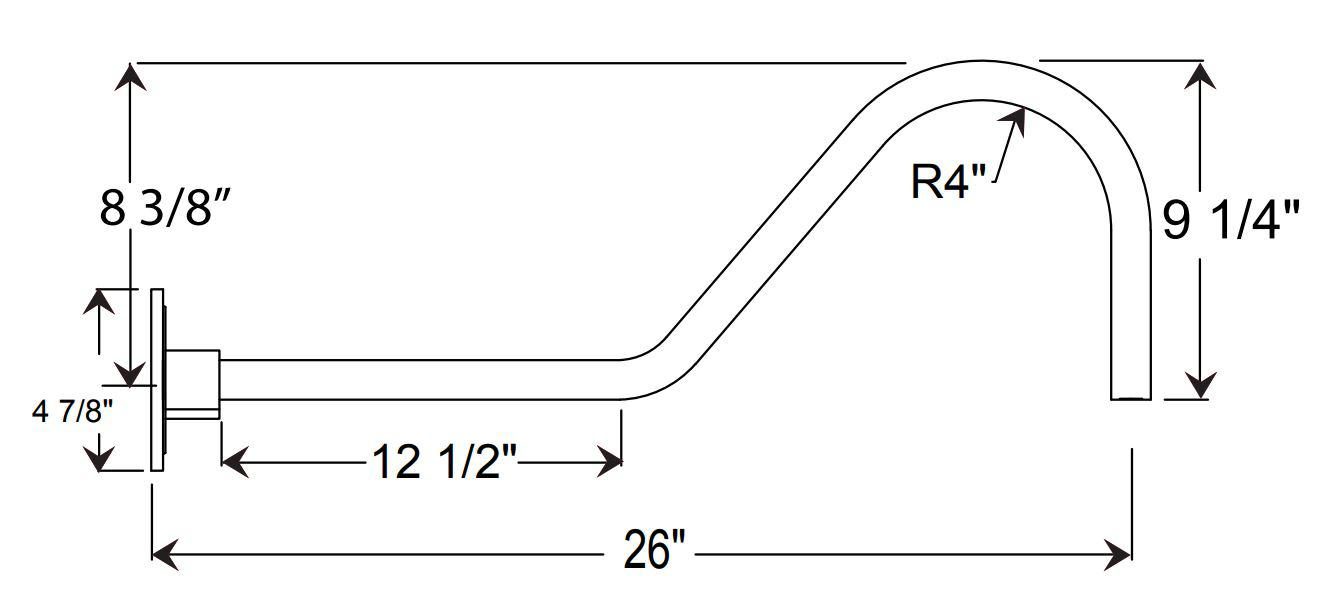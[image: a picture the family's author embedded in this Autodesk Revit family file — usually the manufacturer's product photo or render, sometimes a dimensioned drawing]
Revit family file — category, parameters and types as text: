
# Revit family: OSDC 24,36,42,48 LED
name_source: partatom
category: Lighting Fixtures
units: mm (PartAtom-declared; Revit-internal decimal feet)

## family parameters
Always vertical = Yes
Cut with Voids When Loaded = No
Light Source = Yes
OmniClass Number = 23.80.70.00
OmniClass Title = Lighting
Part Type = Normal
Room Calculation Point = No
Round Connector Dimension = Use Diameter
Shared = No
Work Plane-Based = No

## types (4) — shared parameters
Body Colour = Spun aluminium
Body Material = body
Bulb = Bulb
CRI = >90
Color Filter = 16777215
Construction Material = Heavy Duty spun aluminum.
Default Elevation = 0' - 0"
Description = 120-277 Voltage
Dimming = 1%
Dimming Lamp Color Temperature Shift = <None>
Efficiency = 65-125 lumens per watt
INSIDE BODY = INSIDE BODY
Lamp = LED
Life = L70 50,000 hours
Load Classification = Lighting
Manufacturer = ANP Lighting
Photometric Web File = OSDC48M037LDDW35K.ies
Power Factor = 1
Tilt Angle = 90.00°
URL = https://www.anplighting.com
Voltage = 277 V
Warranty = 5 year limited warranty

## per-type parameters (varying)
| type | Apparent Load | Fixture Diameter | Fixture Height | OSDC24 | OSDC36 | OSDC42 | OSDC48 | Wattage Comments | Weight |
| OSDC24 | 16 VA | 2' - 0" | 0' - 5" | Yes | No | No | No | 16W | 13.0 lbs |
| OSDC36 | 37 VA | 3' - 0" | 0' - 5" | No | Yes | No | No | 37W | 20.0 lbs |
| OSDC42 | 37 VA | 3' - 6" | 0' - 8" | No | No | Yes | No | 37W | 25.0 lbs |
| OSDC48 | 37 VA | 4' - 0" | 0' - 8" | No | No | No | Yes | 37W | 31.0 lbs |

note: column(s) folded — value = type name in every type: Model

## geometry (parser evidence)
native form markers: Sweep x28
no freeform markers — native parametric forms only
